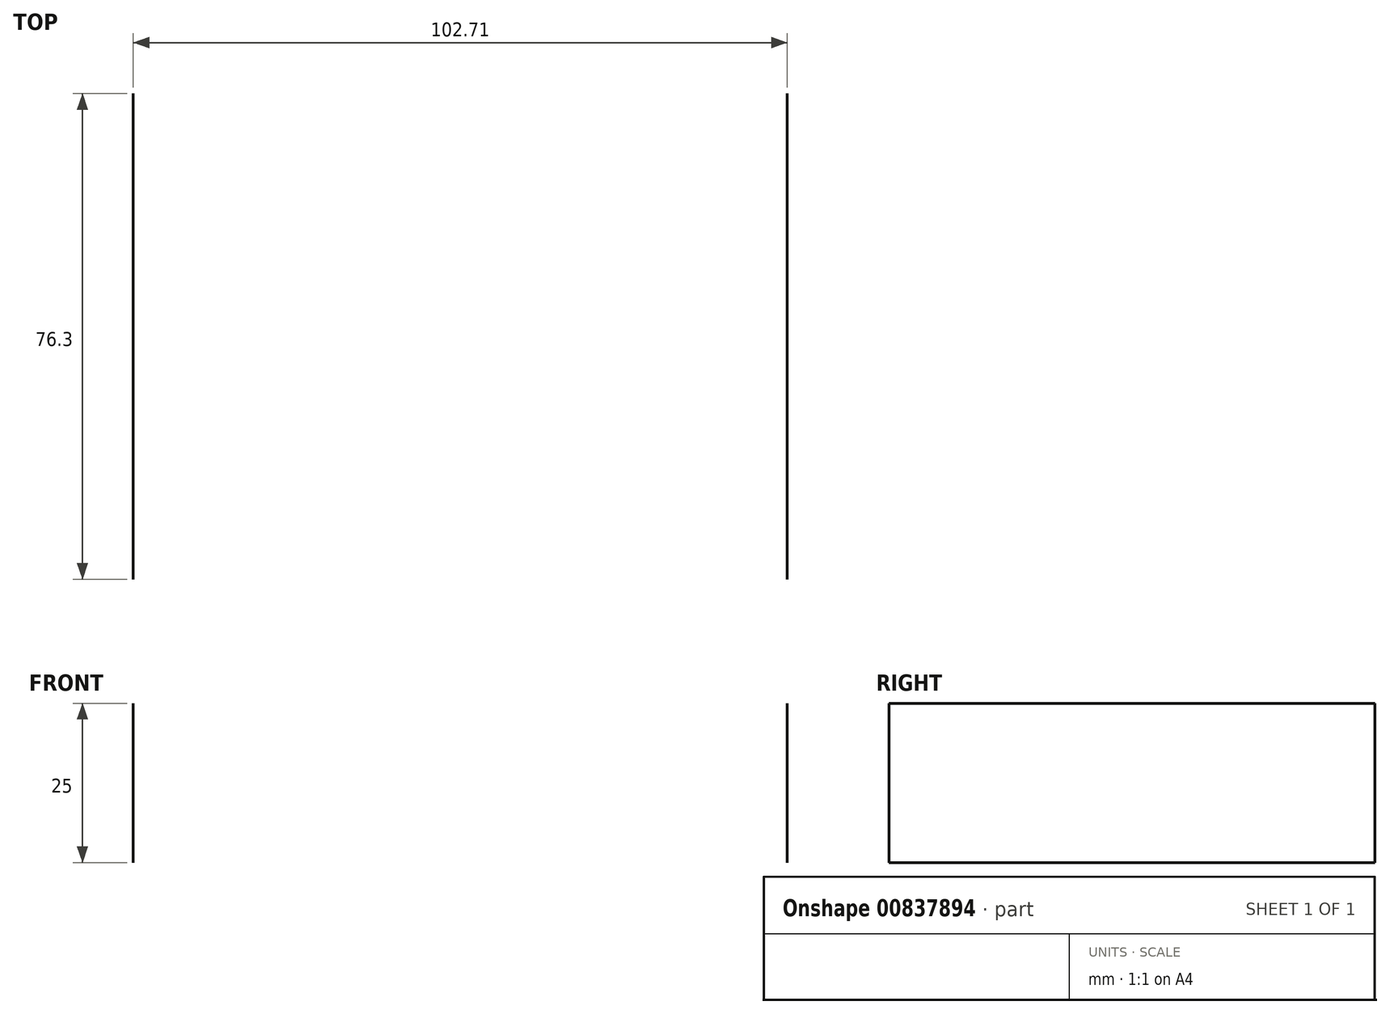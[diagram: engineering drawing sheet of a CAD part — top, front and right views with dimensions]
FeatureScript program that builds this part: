
annotation { "Feature Type Name" : "Feature", "Feature Type Description" : "" }
export const myFeature = defineFeature(function(context is Context, id is Id, definition is map)
    precondition{}
    {
        {
            var Q0;
            Q0=qCreatedBy(makeId("Top.planeOp"),FACE);
            var sketch = newSketch(context, id + "F0", { "sketchPlane" : qUnion([Q0])});
            skLineSegment(sketch, "E0.bottom", {"start": v(-46.8, 33.26) * mm, "end": v(55.92, 33.26) * mm});
            skLineSegment(sketch, "E0.top", {"start": v(-46.8, -43.04) * mm, "end": v(55.92, -43.04) * mm});
            skLineSegment(sketch, "E0.left", {"start": v(-46.8, 33.26) * mm, "end": v(-46.8, -43.04) * mm});
            skLineSegment(sketch, "E0.right", {"start": v(55.92, 33.26) * mm, "end": v(55.92, -43.04) * mm});
            skSolve(sketch);
        }
        {
            var Q0;
            Q0=sQuery(id+"F0.wireOp",EDGE,"E0.left");
            var Q1;
            Q1=sQuery(id+"F0.wireOp",EDGE,"E0.right");
            extrude(context, id + "F1", {"bodyType" : ExtendedToolBodyType.SURFACE, "surfaceEntities" : qUnion([Q0, Q1]), "depth" : 25 * mm, "offsetDistance" : 25 * mm});
        }
    });
